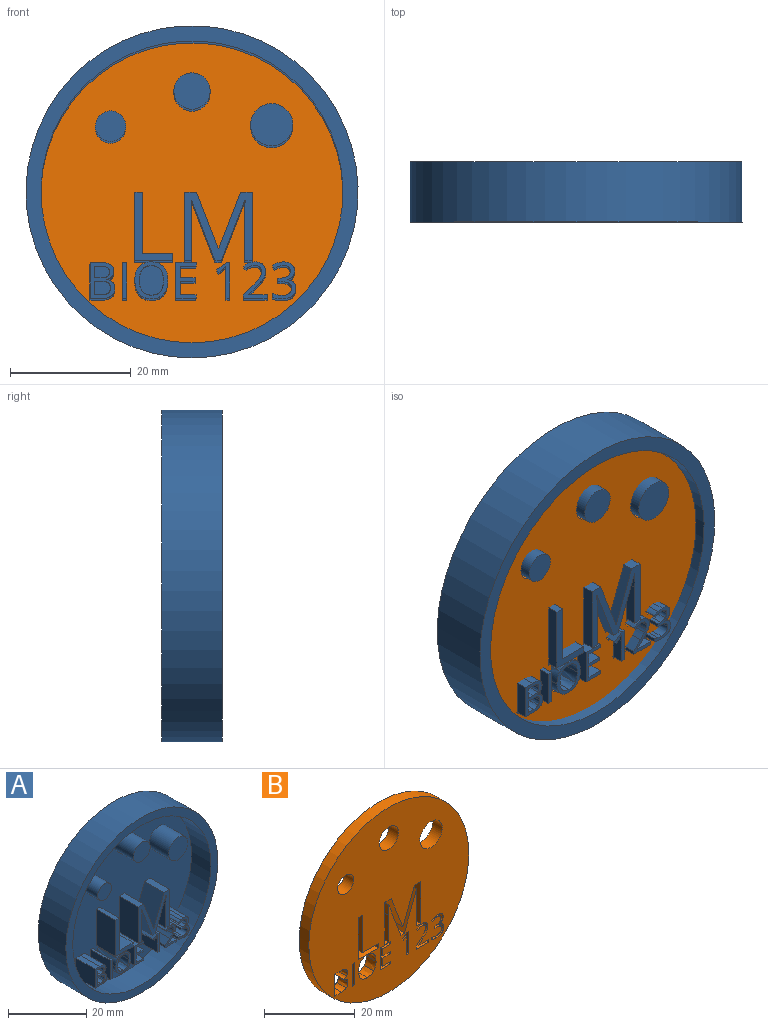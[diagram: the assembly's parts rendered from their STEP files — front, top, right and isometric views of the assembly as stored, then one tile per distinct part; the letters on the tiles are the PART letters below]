
ASSEMBLY  parts=2 mates=1
PART A: 161 faces, bbox 55x10x55 mm
  f0: plane 50x50mm, normal (0,-1,0), area 1717.6mm2, adj f3,f5,f7,f9,f11,f12,f13,f14
  f1: cylinder r=27.5mm len=55mm, axis (0,1,0), area 1727.9mm2, adj f2,f4
  f2: plane 55x55mm, normal (0,1,0), area 2375.8mm2, adj f1
  f3: cylinder r=25mm len=50mm, axis (0,1,0), area 1099.6mm2, adj f0,f4
  f4: plane 55x55mm, normal (0,-1,0), area 412.3mm2, adj f1,f3
  f5: cylinder r=2.5mm len=7mm, axis (0,1,0), area 110mm2, adj f0,f6
  f6: plane 5x5mm, normal (0,-1,0), area 19.6mm2, adj f5
  f7: cylinder r=3mm len=7mm, axis (0,1,0), area 131.9mm2, adj f0,f8
  f8: plane 6x6mm, normal (0,-1,0), area 28.3mm2, adj f7
  f9: cylinder r=3.5mm len=7mm, axis (0,1,0), area 153.9mm2, adj f0,f10
  f10: plane 7x7mm, normal (0,-1,0), area 38.5mm2, adj f9
  f11: plane 11.34x7mm, normal (-1,0,0), area 79.4mm2, adj f0,f12,f16,f17
  f12: plane 7x6.32mm, normal (0,0,-1), area 44.3mm2, adj f0,f11,f13,f17
  f13: plane 7x1.19mm, normal (1,0,0), area 8.4mm2, adj f0,f12,f14,f17
  f14: plane 7x5mm, normal (0,0,1), area 35mm2, adj f0,f13,f15,f17
  f15: plane 10.15x7mm, normal (1,0,0), area 71mm2, adj f0,f14,f16,f17
  f16: plane 7x1.32mm, normal (0,0,1), area 9.2mm2, adj f0,f11,f15,f17
  f17: plane 11.34x6.32mm, normal (0,-1,0), area 20.9mm2, adj f11,f12,f13,f14,f15,f16
  f18: plane 10.05x7mm, normal (-0.93,0,-0.36), area 75.4mm2, adj f0,f19,f35,f36
  f19: plane 7x1.06mm, normal (0,0,-1), area 7.4mm2, adj f0,f18,f20,f36
  f20: plane 10.04x7mm, normal (0.93,0,-0.36), area 75.3mm2, adj f0,f19,f21,f36
  f21: plane 7x0.06mm, normal (0,0,-1), area 0.4mm2, adj f0,f20,f22,f36
  f22: extruded ~7x2.73mm, area 19.1mm2, adj f0,f21,f23,f36
  f23: plane 7.31x7mm, normal (-1,0,0), area 51.2mm2, adj f0,f22,f24,f36
  f24: plane 7x1.32mm, normal (0,0,-1), area 9.2mm2, adj f0,f23,f25,f36
  f25: plane 11.34x7mm, normal (1,0,0), area 79.4mm2, adj f0,f24,f26,f36
  f26: plane 7x1.97mm, normal (0,0,1), area 13.8mm2, adj f0,f25,f27,f36
  f27: plane 9.36x7mm, normal (-0.93,0,0.36), area 70.2mm2, adj f0,f26,f28,f36
  f28: plane 7x0.06mm, normal (0,0,1), area 0.4mm2, adj f0,f27,f29,f36
  f29: plane 9.36x7mm, normal (0.93,0,0.36), area 70.2mm2, adj f0,f28,f30,f36
  f30: plane 7x1.99mm, normal (0,0,1), area 13.9mm2, adj f0,f29,f31,f36
  f31: plane 11.34x7mm, normal (-1,0,0), area 79.4mm2, adj f0,f30,f32,f36
  f32: plane 7x1.22mm, normal (0,0,-1), area 8.5mm2, adj f0,f31,f33,f36
  f33: plane 7.21x7mm, normal (1,0,0), area 50.5mm2, adj f0,f32,f34,f36
  f34: extruded ~7x2.84mm, area 19.9mm2, adj f0,f33,f35,f36
  f35: plane 7x0.06mm, normal (0,0,-1), area 0.4mm2, adj f0,f18,f34,f36
  f36: plane 11.34x11.23mm, normal (0,-1,0), area 55mm2, adj f18,f19,f20,f21,f22,f23,f24,f25
  f37: plane 7x2.23mm, normal (1,0,0), area 15.6mm2, adj f38,f61,f62,f63
  f38: plane 7x1.19mm, normal (0,0,-1), area 8.3mm2, adj f37,f39,f62,f63
  f39: extruded ~7x1.13mm, area 8.3mm2, adj f38,f40,f62,f63
  f40: extruded ~7x0.82mm, area 6.5mm2, adj f39,f41,f62,f63
  f41: extruded ~7x0.88mm, area 6.9mm2, adj f40,f42,f62,f63
  f42: extruded ~7x1.09mm, area 8mm2, adj f41,f61,f62,f63
  f43: plane 7x1.14mm, normal (0,0,1), area 8mm2, adj f44,f59,f62,f64
  f44: plane 7x1.95mm, normal (1,0,0), area 13.7mm2, adj f43,f45,f62,f64
  f45: plane 7x1.02mm, normal (0,0,-1), area 7.1mm2, adj f44,f46,f62,f64
  f46: extruded ~7x1.14mm, area 8.2mm2, adj f45,f47,f62,f64
  f47: extruded ~7x0.72mm, area 5.9mm2, adj f46,f48,f62,f64
  f48: extruded ~7x0.78mm, area 6.1mm2, adj f47,f59,f62,f64
  f49: plane 7x1.68mm, normal (0,0,1), area 11.8mm2, adj f0,f50,f60,f62
  f50: plane 7x5.96mm, normal (-1,0,0), area 41.7mm2, adj f0,f49,f51,f62
  f51: plane 7x2.08mm, normal (0,0,-1), area 14.6mm2, adj f0,f50,f52,f62
  f52: extruded ~7x1.51mm, area 11.3mm2, adj f0,f51,f53,f62
  f53: extruded ~7x1.25mm, area 9.8mm2, adj f0,f52,f54,f62
  f54: extruded ~7x1.43mm, area 15.3mm2, adj f0,f53,f55,f62
  f55: plane 7x0.04mm, normal (1,0,0), area 0.3mm2, adj f0,f54,f56,f62
  f56: extruded ~7x0.86mm, area 6.9mm2, adj f0,f55,f57,f62
  f57: extruded ~7x0.88mm, area 6.6mm2, adj f0,f56,f58,f62
  f58: extruded ~7x1.12mm, area 9.1mm2, adj f0,f57,f60,f62
  f59: extruded ~7x1.06mm, area 7.7mm2, adj f43,f48,f62,f64
  f60: extruded ~7x1.72mm, area 12.4mm2, adj f0,f49,f58,f62
  f61: plane 7x1.24mm, normal (0,0,1), area 8.7mm2, adj f37,f42,f62,f63
  f62: plane 5.96x4.13mm, normal (0,-1,0), area 12.1mm2, adj f37,f38,f39,f40,f41,f42,f43,f44
  f63: plane 2.69x2.23mm, normal (0,-1,0), area 5.5mm2, adj f37,f38,f39,f40,f41,f42,f61
  f64: plane 2.52x1.95mm, normal (0,-1,0), area 4.5mm2, adj f43,f44,f45,f46,f47,f48,f59
  f65: plane 7x5.96mm, normal (-1,0,0), area 41.7mm2, adj f0,f66,f68,f69
  f66: plane 7x0.69mm, normal (0,0,-1), area 4.8mm2, adj f0,f65,f67,f69
  f67: plane 7x5.96mm, normal (1,0,0), area 41.7mm2, adj f0,f66,f68,f69
  f68: plane 7x0.69mm, normal (0,0,1), area 4.8mm2, adj f0,f65,f67,f69
  f69: plane 5.96x0.69mm, normal (0,-1,0), area 4.1mm2, adj f65,f66,f67,f68
  f70: extruded ~7x1.84mm, area 13.6mm2, adj f71,f85,f86,f87
  f71: extruded ~7x1.82mm, area 13.5mm2, adj f70,f72,f86,f87
  f72: extruded ~7x1.51mm, area 11.8mm2, adj f71,f73,f86,f87
  f73: extruded ~7x1.49mm, area 11.7mm2, adj f72,f74,f86,f87
  f74: extruded ~7x1.82mm, area 13.5mm2, adj f73,f75,f86,f87
  f75: extruded ~7x1.84mm, area 13.6mm2, adj f74,f76,f86,f87
  f76: extruded ~7x1.5mm, area 11.7mm2, adj f75,f85,f86,f87
  f77: extruded ~7x2.25mm, area 16.9mm2, adj f0,f78,f84,f86
  f78: extruded ~7x2.25mm, area 16.9mm2, adj f0,f77,f79,f86
  f79: extruded ~7x2.01mm, area 15.6mm2, adj f0,f78,f80,f86
  f80: extruded ~7x2.04mm, area 15.8mm2, adj f0,f79,f81,f86
  f81: extruded ~7x2.26mm, area 17mm2, adj f0,f80,f82,f86
  f82: extruded ~7x2.27mm, area 17.1mm2, adj f0,f81,f83,f86
  f83: extruded ~7x2.03mm, area 15.8mm2, adj f0,f82,f84,f86
  f84: extruded ~7x2.01mm, area 15.7mm2, adj f0,f77,f83,f86
  f85: extruded ~7x1.5mm, area 11.8mm2, adj f70,f76,f86,f87
  f86: plane 6.14x5.48mm, normal (0,-1,0), area 11.2mm2, adj f70,f71,f72,f73,f74,f75,f76,f77
  f87: plane 4.91x4.01mm, normal (0,-1,0), area 16.3mm2, adj f70,f71,f72,f73,f74,f75,f76,f85
  f88: plane 7x3.32mm, normal (0,0,-1), area 23.3mm2, adj f0,f89,f99,f100
  f89: plane 7x0.62mm, normal (1,0,0), area 4.3mm2, adj f0,f88,f90,f100
  f90: plane 7x2.63mm, normal (0,0,1), area 18.4mm2, adj f0,f89,f91,f100
  f91: plane 7x2.19mm, normal (1,0,0), area 15.3mm2, adj f0,f90,f92,f100
  f92: plane 7x2.47mm, normal (0,0,-1), area 17.3mm2, adj f0,f91,f93,f100
  f93: plane 7x0.61mm, normal (1,0,0), area 4.3mm2, adj f0,f92,f94,f100
  f94: plane 7x2.47mm, normal (0,0,1), area 17.3mm2, adj f0,f93,f95,f100
  f95: plane 7x1.92mm, normal (1,0,0), area 13.4mm2, adj f0,f94,f96,f100
  f96: plane 7x2.63mm, normal (0,0,-1), area 18.4mm2, adj f0,f95,f97,f100
  f97: plane 7x0.62mm, normal (1,0,0), area 4.3mm2, adj f0,f96,f98,f100
  f98: plane 7x3.32mm, normal (0,0,1), area 23.3mm2, adj f0,f97,f99,f100
  f99: plane 7x5.96mm, normal (-1,0,0), area 41.7mm2, adj f0,f88,f98,f100
  f100: plane 5.96x3.32mm, normal (0,-1,0), area 8.9mm2, adj f88,f89,f90,f91,f92,f93,f94,f95
  f101: plane 7x0.66mm, normal (0,0,-1), area 4.6mm2, adj f0,f102,f109,f110
  f102: plane 7x5.96mm, normal (1,0,0), area 41.7mm2, adj f0,f101,f103,f110
  f103: plane 7x0.57mm, normal (0,0,1), area 4mm2, adj f0,f102,f104,f110
  f104: plane 7x1.58mm, normal (-0.61,0,0.79), area 14mm2, adj f0,f103,f105,f110
  f105: plane 7x0.46mm, normal (-0.79,0,-0.61), area 4.1mm2, adj f0,f104,f106,f110
  f106: extruded ~7x0.97mm, area 8.8mm2, adj f0,f105,f107,f110
  f107: extruded ~7x0.19mm, area 1.8mm2, adj f0,f106,f108,f110
  f108: extruded ~7x1mm, area 7mm2, adj f0,f107,f109,f110
  f109: plane 7x4.25mm, normal (-1,0,0), area 29.7mm2, adj f0,f101,f108,f110
  f110: plane 5.96x2.15mm, normal (0,-1,0), area 4.9mm2, adj f101,f102,f103,f104,f105,f106,f107,f108
  f111: plane 7x3.92mm, normal (0,0,-1), area 27.4mm2, adj f0,f112,f130,f131
  f112: plane 7x0.63mm, normal (1,0,0), area 4.4mm2, adj f0,f111,f113,f131
  f113: plane 7x3.07mm, normal (0,0,1), area 21.5mm2, adj f0,f112,f114,f131
  f114: plane 7x0.03mm, normal (1,0,0), area 0.2mm2, adj f0,f113,f115,f131
  f115: plane 7x1.3mm, normal (0.7,0,-0.71), area 12.8mm2, adj f0,f114,f116,f131
  f116: extruded ~7x1.4mm, area 12.9mm2, adj f0,f115,f117,f131
  f117: extruded ~7x1.12mm, area 8.3mm2, adj f0,f116,f118,f131
  f118: extruded ~7x1.16mm, area 9mm2, adj f0,f117,f119,f131
  f119: extruded ~7x1.32mm, area 9.9mm2, adj f0,f118,f120,f131
  f120: extruded ~7x1.79mm, area 13.7mm2, adj f0,f119,f121,f131
  f121: plane 7x0.46mm, normal (-0.79,0,-0.61), area 4.1mm2, adj f0,f120,f122,f131
  f122: extruded ~7x0.74mm, area 6.1mm2, adj f0,f121,f123,f131
  f123: extruded ~7x0.7mm, area 5mm2, adj f0,f122,f124,f131
  f124: extruded ~7x0.8mm, area 6.1mm2, adj f0,f123,f125,f131
  f125: extruded ~7x0.76mm, area 5.8mm2, adj f0,f124,f126,f131
  f126: extruded ~7x0.63mm, area 4.5mm2, adj f0,f125,f127,f131
  f127: extruded ~7x0.6mm, area 4.9mm2, adj f0,f126,f128,f131
  f128: extruded ~7x1.04mm, area 9.8mm2, adj f0,f127,f129,f131
  f129: plane 7x1.58mm, normal (-0.71,0,0.71), area 15.6mm2, adj f0,f128,f130,f131
  f130: plane 7x0.58mm, normal (-1,0,0), area 4.1mm2, adj f0,f111,f129,f131
  f131: plane 6.04x3.92mm, normal (0,-1,0), area 7.8mm2, adj f111,f112,f113,f114,f115,f116,f117,f118
  f132: extruded ~7x0.93mm, area 7.1mm2, adj f0,f133,f159,f160
  f133: extruded ~7x1.09mm, area 8.6mm2, adj f0,f132,f134,f160
  f134: extruded ~7x1.35mm, area 10mm2, adj f0,f133,f135,f160
  f135: extruded ~7x1.01mm, area 7.2mm2, adj f0,f134,f136,f160
  f136: extruded ~7x0.85mm, area 6.7mm2, adj f0,f135,f137,f160
  f137: plane 7x0.46mm, normal (-0.8,0,-0.6), area 4mm2, adj f0,f136,f138,f160
  f138: extruded ~7x0.79mm, area 6.2mm2, adj f0,f137,f139,f160
  f139: extruded ~7x0.74mm, area 5.2mm2, adj f0,f138,f140,f160
  f140: extruded ~7x0.81mm, area 6.1mm2, adj f0,f139,f141,f160
  f141: extruded ~7x0.68mm, area 5.4mm2, adj f0,f140,f142,f160
  f142: extruded ~7x0.85mm, area 6.9mm2, adj f0,f141,f143,f160
  f143: extruded ~7x1.1mm, area 8.2mm2, adj f0,f142,f144,f160
  f144: plane 7x0.59mm, normal (0,0,1), area 4.2mm2, adj f0,f143,f145,f160
  f145: plane 7x0.58mm, normal (-1,0,0), area 4.1mm2, adj f0,f144,f146,f160
  f146: plane 7x0.59mm, normal (0,0,-1), area 4.1mm2, adj f0,f145,f147,f160
  f147: extruded ~7x1.7mm, area 16mm2, adj f0,f146,f148,f160
  f148: extruded ~7x1.54mm, area 15.7mm2, adj f0,f147,f149,f160
  f149: extruded ~7x0.83mm, area 5.9mm2, adj f0,f148,f150,f160
  f150: extruded ~7x0.83mm, area 6.1mm2, adj f0,f149,f151,f160
  f151: plane 7x0.64mm, normal (-1,0,0), area 4.5mm2, adj f0,f150,f152,f160
  f152: extruded ~7x0.76mm, area 5.6mm2, adj f0,f151,f153,f160
  f153: extruded ~7x0.87mm, area 6.1mm2, adj f0,f152,f154,f160
  f154: extruded ~7x1.68mm, area 12.4mm2, adj f0,f153,f155,f160
  f155: extruded ~7x1.31mm, area 10.4mm2, adj f0,f154,f156,f160
  f156: extruded ~7x0.96mm, area 7.3mm2, adj f0,f155,f157,f160
  f157: extruded ~7x1.06mm, area 8.3mm2, adj f0,f156,f158,f160
  f158: plane 7x0.03mm, normal (1,0,0), area 0.2mm2, adj f0,f157,f159,f160
  f159: extruded ~7x0.91mm, area 7.3mm2, adj f0,f132,f158,f160
  f160: plane 6.13x3.9mm, normal (0,-1,0), area 8.2mm2, adj f132,f133,f134,f135,f136,f137,f138,f139
PART B: 122 faces, bbox 50x3x50 mm
  f0: plane 11.34x3mm, normal (1,0,0), area 34mm2, adj f1,f110,f120,f121
  f1: plane 3x1.32mm, normal (0,0,-1), area 4mm2, adj f0,f2,f120,f121
  f2: plane 10.15x3mm, normal (-1,0,0), area 30.4mm2, adj f1,f3,f120,f121
  f3: plane 5x3mm, normal (0,0,-1), area 15mm2, adj f2,f4,f120,f121
  f4: plane 3x1.19mm, normal (-1,0,0), area 3.6mm2, adj f3,f110,f120,f121
  f5: plane 10.05x3.85mm, normal (0.93,0,0.36), area 32.3mm2, adj f6,f111,f120,f121
  f6: plane 3x0.06mm, normal (0,0,1), area 0.2mm2, adj f5,f7,f120,f121
  f7: extruded ~3x2.84mm, area 8.5mm2, adj f6,f8,f120,f121
  f8: plane 7.21x3mm, normal (-1,0,0), area 21.6mm2, adj f7,f9,f120,f121
  f9: plane 3x1.22mm, normal (0,0,1), area 3.7mm2, adj f8,f10,f120,f121
  f10: plane 11.34x3mm, normal (1,0,0), area 34mm2, adj f9,f11,f120,f121
  f11: plane 3x1.99mm, normal (0,0,-1), area 6mm2, adj f10,f12,f120,f121
  f12: plane 9.36x3.59mm, normal (-0.93,0,-0.36), area 30.1mm2, adj f11,f13,f120,f121
  f13: plane 3x0.06mm, normal (0,0,-1), area 0.2mm2, adj f12,f14,f120,f121
  f14: plane 9.36x3.62mm, normal (0.93,0,-0.36), area 30.1mm2, adj f13,f15,f120,f121
  f15: plane 3x1.97mm, normal (0,0,-1), area 5.9mm2, adj f14,f16,f120,f121
  f16: plane 11.34x3mm, normal (-1,0,0), area 34mm2, adj f15,f17,f120,f121
  f17: plane 3x1.32mm, normal (0,0,1), area 4mm2, adj f16,f18,f120,f121
  f18: plane 7.31x3mm, normal (1,0,0), area 21.9mm2, adj f17,f19,f120,f121
  f19: extruded ~3x2.73mm, area 8.2mm2, adj f18,f20,f120,f121
  f20: plane 3x0.06mm, normal (0,0,1), area 0.2mm2, adj f19,f21,f120,f121
  f21: plane 10.04x3.88mm, normal (-0.93,0,0.36), area 32.3mm2, adj f20,f111,f120,f121
  f22: plane 3x1.68mm, normal (0,0,-1), area 5.1mm2, adj f23,f112,f120,f121
  f23: extruded ~3x1.72mm, area 5.3mm2, adj f22,f24,f120,f121
  f24: extruded ~3x1.12mm, area 3.9mm2, adj f23,f25,f120,f121
  f25: extruded ~3x0.88mm, area 2.8mm2, adj f24,f26,f120,f121
  f26: extruded ~3x0.86mm, area 3mm2, adj f25,f27,f120,f121
  f27: plane 3x0.04mm, normal (-1,0,0), area 0.1mm2, adj f26,f28,f120,f121
  f28: extruded ~3x1.43mm, area 6.5mm2, adj f27,f29,f120,f121
  f29: extruded ~3x1.25mm, area 4.2mm2, adj f28,f30,f120,f121
  f30: extruded ~3x1.51mm, area 4.8mm2, adj f29,f31,f120,f121
  f31: plane 3x2.08mm, normal (0,0,1), area 6.2mm2, adj f30,f112,f120,f121
  f32: plane 5.96x3mm, normal (1,0,0), area 17.9mm2, adj f33,f113,f120,f121
  f33: plane 3x0.69mm, normal (0,0,-1), area 2.1mm2, adj f32,f34,f120,f121
  f34: plane 5.96x3mm, normal (-1,0,0), area 17.9mm2, adj f33,f113,f120,f121
  f35: extruded ~3x2.25mm, area 7.3mm2, adj f36,f114,f120,f121
  f36: extruded ~3x2.01mm, area 6.7mm2, adj f35,f37,f120,f121
  f37: extruded ~3x2.03mm, area 6.8mm2, adj f36,f38,f120,f121
  f38: extruded ~3x2.27mm, area 7.3mm2, adj f37,f39,f120,f121
  f39: extruded ~3x2.26mm, area 7.3mm2, adj f38,f40,f120,f121
  f40: extruded ~3x2.04mm, area 6.8mm2, adj f39,f41,f120,f121
  f41: extruded ~3x2.01mm, area 6.7mm2, adj f40,f114,f120,f121
  f42: plane 3.32x3mm, normal (0,0,1), area 10mm2, adj f43,f115,f120,f121
  f43: plane 5.96x3mm, normal (1,0,0), area 17.9mm2, adj f42,f44,f120,f121
  f44: plane 3.32x3mm, normal (0,0,-1), area 10mm2, adj f43,f45,f120,f121
  f45: plane 3x0.62mm, normal (-1,0,0), area 1.8mm2, adj f44,f46,f120,f121
  f46: plane 3x2.63mm, normal (0,0,1), area 7.9mm2, adj f45,f47,f120,f121
  f47: plane 3x1.92mm, normal (-1,0,0), area 5.8mm2, adj f46,f48,f120,f121
  f48: plane 3x2.47mm, normal (0,0,-1), area 7.4mm2, adj f47,f49,f120,f121
  f49: plane 3x0.61mm, normal (-1,0,0), area 1.8mm2, adj f48,f50,f120,f121
  f50: plane 3x2.47mm, normal (0,0,1), area 7.4mm2, adj f49,f51,f120,f121
  f51: plane 3x2.19mm, normal (-1,0,0), area 6.6mm2, adj f50,f52,f120,f121
  f52: plane 3x2.63mm, normal (0,0,-1), area 7.9mm2, adj f51,f115,f120,f121
  f53: plane 3x0.66mm, normal (0,0,1), area 2mm2, adj f54,f116,f120,f121
  f54: plane 4.25x3mm, normal (1,0,0), area 12.7mm2, adj f53,f55,f120,f121
  f55: extruded ~3x1mm, area 3mm2, adj f54,f56,f120,f121
  f56: extruded ~3x0.19mm, area 0.8mm2, adj f55,f57,f120,f121
  f57: extruded ~3x0.97mm, area 3.8mm2, adj f56,f58,f120,f121
  f58: plane 3x0.46mm, normal (0.79,0,0.61), area 1.8mm2, adj f57,f59,f120,f121
  f59: plane 3x1.58mm, normal (0.61,0,-0.79), area 6mm2, adj f58,f60,f120,f121
  f60: plane 3x0.57mm, normal (0,0,-1), area 1.7mm2, adj f59,f116,f120,f121
  f61: plane 3.92x3mm, normal (0,0,1), area 11.7mm2, adj f62,f117,f120,f121
  f62: plane 3x0.58mm, normal (1,0,0), area 1.7mm2, adj f61,f63,f120,f121
  f63: plane 3x1.58mm, normal (0.71,0,-0.71), area 6.7mm2, adj f62,f64,f120,f121
  f64: extruded ~3x1.04mm, area 4.2mm2, adj f63,f65,f120,f121
  f65: extruded ~3x0.6mm, area 2.1mm2, adj f64,f66,f120,f121
  f66: extruded ~3x0.63mm, area 1.9mm2, adj f65,f67,f120,f121
  f67: extruded ~3x0.76mm, area 2.5mm2, adj f66,f68,f120,f121
  f68: extruded ~3x0.8mm, area 2.6mm2, adj f67,f69,f120,f121
  f69: extruded ~3x0.7mm, area 2.2mm2, adj f68,f70,f120,f121
  f70: extruded ~3x0.74mm, area 2.6mm2, adj f69,f71,f120,f121
  f71: plane 3x0.46mm, normal (0.79,0,0.61), area 1.8mm2, adj f70,f72,f120,f121
  f72: extruded ~3x1.79mm, area 5.9mm2, adj f71,f73,f120,f121
  f73: extruded ~3x1.32mm, area 4.3mm2, adj f72,f74,f120,f121
  f74: extruded ~3x1.16mm, area 3.9mm2, adj f73,f75,f120,f121
  f75: extruded ~3x1.12mm, area 3.5mm2, adj f74,f76,f120,f121
  f76: extruded ~3x1.4mm, area 5.5mm2, adj f75,f77,f120,f121
  f77: plane 3x1.3mm, normal (-0.7,0,0.71), area 5.5mm2, adj f76,f78,f120,f121
  f78: plane 3x0.03mm, normal (-1,0,0), area 0.1mm2, adj f77,f79,f120,f121
  f79: plane 3.07x3mm, normal (0,0,-1), area 9.2mm2, adj f78,f117,f120,f121
  f80: extruded ~3x0.93mm, area 3mm2, adj f81,f118,f120,f121
  f81: extruded ~3x0.91mm, area 3.1mm2, adj f80,f82,f120,f121
  f82: plane 3x0.03mm, normal (-1,0,0), area 0.1mm2, adj f81,f83,f120,f121
  f83: extruded ~3x1.06mm, area 3.5mm2, adj f82,f84,f120,f121
  f84: extruded ~3x0.96mm, area 3.1mm2, adj f83,f85,f120,f121
  f85: extruded ~3x1.31mm, area 4.5mm2, adj f84,f86,f120,f121
  f86: extruded ~3x1.68mm, area 5.3mm2, adj f85,f87,f120,f121
  f87: extruded ~3x0.87mm, area 2.6mm2, adj f86,f88,f120,f121
  f88: extruded ~3x0.76mm, area 2.4mm2, adj f87,f89,f120,f121
  f89: plane 3x0.64mm, normal (1,0,0), area 1.9mm2, adj f88,f90,f120,f121
  f90: extruded ~3x0.83mm, area 2.6mm2, adj f89,f91,f120,f121
  f91: extruded ~3x0.83mm, area 2.5mm2, adj f90,f92,f120,f121
  f92: extruded ~3x1.54mm, area 6.7mm2, adj f91,f93,f120,f121
  f93: extruded ~3x1.7mm, area 6.9mm2, adj f92,f94,f120,f121
  f94: plane 3x0.59mm, normal (0,0,1), area 1.8mm2, adj f93,f95,f120,f121
  f95: plane 3x0.58mm, normal (1,0,0), area 1.7mm2, adj f94,f96,f120,f121
  f96: plane 3x0.59mm, normal (0,0,-1), area 1.8mm2, adj f95,f97,f120,f121
  f97: extruded ~3x1.1mm, area 3.5mm2, adj f96,f98,f120,f121
  f98: extruded ~3x0.85mm, area 3mm2, adj f97,f99,f120,f121
  f99: extruded ~3x0.68mm, area 2.3mm2, adj f98,f100,f120,f121
  f100: extruded ~3x0.81mm, area 2.6mm2, adj f99,f101,f120,f121
  f101: extruded ~3x0.74mm, area 2.2mm2, adj f100,f102,f120,f121
  f102: extruded ~3x0.79mm, area 2.7mm2, adj f101,f103,f120,f121
  f103: plane 3x0.46mm, normal (0.8,0,0.6), area 1.7mm2, adj f102,f104,f120,f121
  f104: extruded ~3x0.85mm, area 2.9mm2, adj f103,f105,f120,f121
  f105: extruded ~3x1.01mm, area 3.1mm2, adj f104,f106,f120,f121
  f106: extruded ~3x1.35mm, area 4.3mm2, adj f105,f118,f120,f121
  f107: cylinder r=2.5mm len=5mm, axis (0,1,0), area 47.1mm2, adj f120,f121
  f108: cylinder r=3mm len=6mm, axis (0,1,0), area 56.5mm2, adj f120,f121
  f109: cylinder r=3.5mm len=7mm, axis (0,1,0), area 66mm2, adj f120,f121
  f110: plane 6.32x3mm, normal (0,0,1), area 19mm2, adj f0,f4,f120,f121
  f111: plane 3x1.06mm, normal (0,0,1), area 3.2mm2, adj f5,f21,f120,f121
  f112: plane 5.96x3mm, normal (1,0,0), area 17.9mm2, adj f22,f31,f120,f121
  f113: plane 3x0.69mm, normal (0,0,1), area 2.1mm2, adj f32,f34,f120,f121
  f114: extruded ~3x2.25mm, area 7.2mm2, adj f35,f41,f120,f121
  f115: plane 3x0.62mm, normal (-1,0,0), area 1.9mm2, adj f42,f52,f120,f121
  f116: plane 5.96x3mm, normal (-1,0,0), area 17.9mm2, adj f53,f60,f120,f121
  f117: plane 3x0.63mm, normal (-1,0,0), area 1.9mm2, adj f61,f79,f120,f121
  f118: extruded ~3x1.09mm, area 3.7mm2, adj f80,f106,f120,f121
  f119: cylinder r=25mm len=50mm, axis (0,1,0), area 471.2mm2, adj f120,f121
  f120: plane 50x50mm, normal (0,-1,0), area 1717.6mm2, adj f0,f1,f2,f3,f4,f5,f6,f7
  f121: plane 50x50mm, normal (0,1,0), area 1717.6mm2, adj f0,f1,f2,f3,f4,f5,f6,f7
PLACE A rot(axis=(-0.57,-0.33,0.75),0deg) t=(-32.25,-40.47,-0.29)mm
PLACE B rot(axis=(-0.57,-0.33,0.75),0deg) t=(-32.26,-42.57,-0.62)mm
MATE slider B.f120 <-> A.f1  axis (0,-1,0) through (-32.25,-48.57,-0.29)mm
